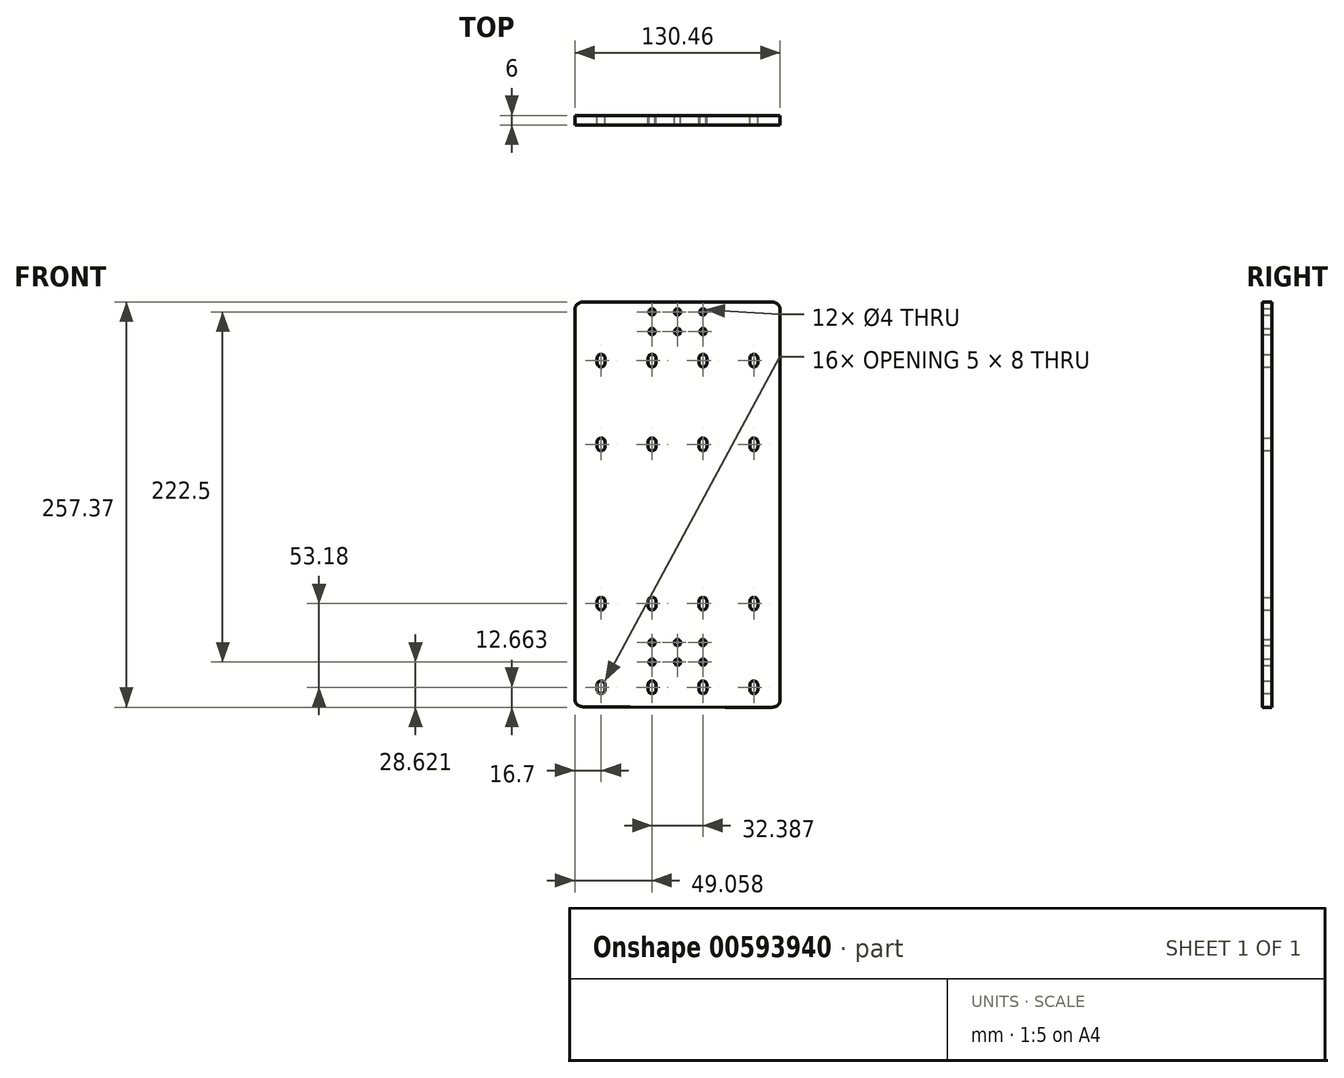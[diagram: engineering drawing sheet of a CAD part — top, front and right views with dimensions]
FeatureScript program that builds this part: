
annotation { "Feature Type Name" : "Feature", "Feature Type Description" : "" }
export const myFeature = defineFeature(function(context is Context, id is Id, definition is map)
    precondition{}
    {
        {
            var Q0;
            Q0=qCreatedBy(makeId("Front.planeOp"),FACE);
            var sketch = newSketch(context, id + "F0", { "sketchPlane" : qUnion([Q0])});
            skLineSegment(sketch, "E0.bottom", {"start": v(-82.55, 112.46) * mm, "end": v(-203.01, 112.46) * mm});
            skCircle(sketch, "E1", {"center": v(-142.78, 106.21) * mm, "radius": 2 * mm});
            skPoint(sketch, "E1.centerSnap0", {"position": v(-142.78, 112.46) * mm});
            skPoint(sketch, "E1.centerSnap1", {"position": v(-97.78, 99.96) * mm});
            skCircle(sketch, "E2.1.0.0", {"center": v(-126.61, 106.21) * mm, "radius": 2 * mm});
            skLineSegment(sketch, "E2.direction1", {"start": v(-142.78, 106.21) * mm, "end": v(-126.61, 106.21) * mm, "construction": true});
            skCircle(sketch, "E3.1.0.0", {"center": v(-158.95, 106.21) * mm, "radius": 2 * mm});
            skLineSegment(sketch, "E3.direction1", {"start": v(-142.78, 106.21) * mm, "end": v(-158.95, 106.21) * mm, "construction": true});
            skPoint(sketch, "E4", {"position": v(-97.78, 112.46) * mm});
            skCircle(sketch, "E5.2.1.0", {"center": v(-126.56, 93.71) * mm, "radius": 2 * mm});
            skCircle(sketch, "E5.2.1.1", {"center": v(-142.73, 93.71) * mm, "radius": 2 * mm});
            skCircle(sketch, "E5.2.1.2", {"center": v(-158.95, 93.71) * mm, "radius": 2 * mm});
            skLineSegment(sketch, "E5.direction1", {"start": v(-149.11, 106.21) * mm, "end": v(-149.11, 106.21) * mm});
            skLineSegment(sketch, "E5.direction2", {"start": v(-126.61, 106.21) * mm, "end": v(-126.56, 93.71) * mm, "construction": true});
            skLineSegment(sketch, "E6.bottom", {"start": v(-94.18, 79.25) * mm, "end": v(-94.4, 79.25) * mm});
            skLineSegment(sketch, "E6.top", {"start": v(-94.18, 71.25) * mm, "end": v(-94.4, 71.25) * mm});
            skLineSegment(sketch, "E6.left", {"start": v(-91.8, 76.87) * mm, "end": v(-91.8, 73.64) * mm});
            skLineSegment(sketch, "E6.right", {"start": v(-96.8, 76.87) * mm, "end": v(-96.8, 73.64) * mm});
            skPoint(sketch, "E7.visualSharp", {"position": v(-91.8, 79.25) * mm});
            skArc(sketch, "E7.filletArc", {"start": v(-91.8, 76.87) * mm, "mid": v(-92.49, 78.55) * mm, "end": v(-94.18, 79.25) * mm});
            skPoint(sketch, "E8.visualSharp", {"position": v(-91.8, 71.25) * mm});
            skArc(sketch, "E8.filletArc", {"start": v(-94.18, 71.25) * mm, "mid": v(-92.49, 71.95) * mm, "end": v(-91.8, 73.64) * mm});
            skPoint(sketch, "E9.visualSharp", {"position": v(-96.8, 71.25) * mm});
            skArc(sketch, "E9.filletArc", {"start": v(-96.8, 73.64) * mm, "mid": v(-96.1, 71.95) * mm, "end": v(-94.4, 71.25) * mm});
            skPoint(sketch, "E10.visualSharp", {"position": v(-96.8, 79.25) * mm});
            skArc(sketch, "E10.filletArc", {"start": v(-94.4, 79.25) * mm, "mid": v(-96.1, 78.55) * mm, "end": v(-96.8, 76.87) * mm});
            skPoint(sketch, "E11.0.1.0", {"position": v(-91.8, 26.07) * mm});
            skArc(sketch, "E11.0.1.1", {"start": v(-96.8, 20.46) * mm, "mid": v(-96.1, 18.77) * mm, "end": v(-94.4, 18.07) * mm});
            skArc(sketch, "E11.0.1.2", {"start": v(-91.8, 23.69) * mm, "mid": v(-92.49, 25.37) * mm, "end": v(-94.18, 26.07) * mm});
            skArc(sketch, "E11.0.1.3", {"start": v(-94.4, 26.07) * mm, "mid": v(-96.1, 25.37) * mm, "end": v(-96.8, 23.69) * mm});
            skPoint(sketch, "E11.0.1.4", {"position": v(-91.8, 18.07) * mm});
            skPoint(sketch, "E11.0.1.5", {"position": v(-96.8, 18.07) * mm});
            skLineSegment(sketch, "E11.0.1.6", {"start": v(-96.8, 23.69) * mm, "end": v(-96.8, 20.46) * mm});
            skArc(sketch, "E11.0.1.7", {"start": v(-94.18, 18.07) * mm, "mid": v(-92.49, 18.77) * mm, "end": v(-91.8, 20.46) * mm});
            skPoint(sketch, "E11.0.1.8", {"position": v(-96.8, 26.07) * mm});
            skLineSegment(sketch, "E11.0.1.9", {"start": v(-91.8, 23.69) * mm, "end": v(-91.8, 20.46) * mm});
            skLineSegment(sketch, "E11.0.1.10", {"start": v(-94.18, 18.07) * mm, "end": v(-94.4, 18.07) * mm});
            skLineSegment(sketch, "E11.0.1.11", {"start": v(-94.18, 26.07) * mm, "end": v(-94.4, 26.07) * mm});
            skPoint(sketch, "E11.1.0.0", {"position": v(-124.13, 79.25) * mm});
            skArc(sketch, "E11.1.0.1", {"start": v(-129.13, 73.64) * mm, "mid": v(-128.43, 71.95) * mm, "end": v(-126.74, 71.25) * mm});
            skArc(sketch, "E11.1.0.2", {"start": v(-124.13, 76.87) * mm, "mid": v(-124.83, 78.55) * mm, "end": v(-126.52, 79.25) * mm});
            skArc(sketch, "E11.1.0.3", {"start": v(-126.74, 79.25) * mm, "mid": v(-128.43, 78.55) * mm, "end": v(-129.13, 76.87) * mm});
            skPoint(sketch, "E11.1.0.4", {"position": v(-124.13, 71.25) * mm});
            skPoint(sketch, "E11.1.0.5", {"position": v(-129.13, 71.25) * mm});
            skLineSegment(sketch, "E11.1.0.6", {"start": v(-129.13, 76.87) * mm, "end": v(-129.13, 73.64) * mm});
            skArc(sketch, "E11.1.0.7", {"start": v(-126.52, 71.25) * mm, "mid": v(-124.83, 71.95) * mm, "end": v(-124.13, 73.64) * mm});
            skPoint(sketch, "E11.1.0.8", {"position": v(-129.13, 79.25) * mm});
            skLineSegment(sketch, "E11.1.0.9", {"start": v(-124.13, 76.87) * mm, "end": v(-124.13, 73.64) * mm});
            skLineSegment(sketch, "E11.1.0.10", {"start": v(-126.52, 71.25) * mm, "end": v(-126.74, 71.25) * mm});
            skLineSegment(sketch, "E11.1.0.11", {"start": v(-126.52, 79.25) * mm, "end": v(-126.74, 79.25) * mm});
            skPoint(sketch, "E11.1.1.0", {"position": v(-124.13, 26.07) * mm});
            skArc(sketch, "E11.1.1.1", {"start": v(-129.13, 20.46) * mm, "mid": v(-128.43, 18.77) * mm, "end": v(-126.74, 18.07) * mm});
            skArc(sketch, "E11.1.1.2", {"start": v(-124.13, 23.69) * mm, "mid": v(-124.83, 25.37) * mm, "end": v(-126.52, 26.07) * mm});
            skArc(sketch, "E11.1.1.3", {"start": v(-126.74, 26.07) * mm, "mid": v(-128.43, 25.37) * mm, "end": v(-129.13, 23.69) * mm});
            skPoint(sketch, "E11.1.1.4", {"position": v(-124.13, 18.07) * mm});
            skPoint(sketch, "E11.1.1.5", {"position": v(-129.13, 18.07) * mm});
            skLineSegment(sketch, "E11.1.1.6", {"start": v(-129.13, 23.69) * mm, "end": v(-129.13, 20.46) * mm});
            skArc(sketch, "E11.1.1.7", {"start": v(-126.52, 18.07) * mm, "mid": v(-124.83, 18.77) * mm, "end": v(-124.13, 20.46) * mm});
            skPoint(sketch, "E11.1.1.8", {"position": v(-129.13, 26.07) * mm});
            skLineSegment(sketch, "E11.1.1.9", {"start": v(-124.13, 23.69) * mm, "end": v(-124.13, 20.46) * mm});
            skLineSegment(sketch, "E11.1.1.10", {"start": v(-126.52, 18.07) * mm, "end": v(-126.74, 18.07) * mm});
            skLineSegment(sketch, "E11.1.1.11", {"start": v(-126.52, 26.07) * mm, "end": v(-126.74, 26.07) * mm});
            skPoint(sketch, "E11.2.0.0", {"position": v(-156.47, 79.25) * mm});
            skArc(sketch, "E11.2.0.1", {"start": v(-161.47, 73.64) * mm, "mid": v(-160.77, 71.95) * mm, "end": v(-159.08, 71.25) * mm});
            skArc(sketch, "E11.2.0.2", {"start": v(-156.47, 76.87) * mm, "mid": v(-157.17, 78.55) * mm, "end": v(-158.86, 79.25) * mm});
            skArc(sketch, "E11.2.0.3", {"start": v(-159.08, 79.25) * mm, "mid": v(-160.77, 78.55) * mm, "end": v(-161.47, 76.87) * mm});
            skPoint(sketch, "E11.2.0.4", {"position": v(-156.47, 71.25) * mm});
            skPoint(sketch, "E11.2.0.5", {"position": v(-161.47, 71.25) * mm});
            skLineSegment(sketch, "E11.2.0.6", {"start": v(-161.47, 76.87) * mm, "end": v(-161.47, 73.64) * mm});
            skArc(sketch, "E11.2.0.7", {"start": v(-158.86, 71.25) * mm, "mid": v(-157.17, 71.95) * mm, "end": v(-156.47, 73.64) * mm});
            skPoint(sketch, "E11.2.0.8", {"position": v(-161.47, 79.25) * mm});
            skLineSegment(sketch, "E11.2.0.9", {"start": v(-156.47, 76.87) * mm, "end": v(-156.47, 73.64) * mm});
            skLineSegment(sketch, "E11.2.0.10", {"start": v(-158.86, 71.25) * mm, "end": v(-159.08, 71.25) * mm});
            skLineSegment(sketch, "E11.2.0.11", {"start": v(-158.86, 79.25) * mm, "end": v(-159.08, 79.25) * mm});
            skPoint(sketch, "E11.2.1.0", {"position": v(-156.47, 26.07) * mm});
            skArc(sketch, "E11.2.1.1", {"start": v(-161.47, 20.46) * mm, "mid": v(-160.77, 18.77) * mm, "end": v(-159.08, 18.07) * mm});
            skArc(sketch, "E11.2.1.2", {"start": v(-156.47, 23.69) * mm, "mid": v(-157.17, 25.37) * mm, "end": v(-158.86, 26.07) * mm});
            skArc(sketch, "E11.2.1.3", {"start": v(-159.08, 26.07) * mm, "mid": v(-160.77, 25.37) * mm, "end": v(-161.47, 23.69) * mm});
            skPoint(sketch, "E11.2.1.4", {"position": v(-156.47, 18.07) * mm});
            skPoint(sketch, "E11.2.1.5", {"position": v(-161.47, 18.07) * mm});
            skLineSegment(sketch, "E11.2.1.6", {"start": v(-161.47, 23.69) * mm, "end": v(-161.47, 20.46) * mm});
            skArc(sketch, "E11.2.1.7", {"start": v(-158.86, 18.07) * mm, "mid": v(-157.17, 18.77) * mm, "end": v(-156.47, 20.46) * mm});
            skPoint(sketch, "E11.2.1.8", {"position": v(-161.47, 26.07) * mm});
            skLineSegment(sketch, "E11.2.1.9", {"start": v(-156.47, 23.69) * mm, "end": v(-156.47, 20.46) * mm});
            skLineSegment(sketch, "E11.2.1.10", {"start": v(-158.86, 18.07) * mm, "end": v(-159.08, 18.07) * mm});
            skLineSegment(sketch, "E11.2.1.11", {"start": v(-158.86, 26.07) * mm, "end": v(-159.08, 26.07) * mm});
            skPoint(sketch, "E11.3.0.0", {"position": v(-188.81, 79.25) * mm});
            skArc(sketch, "E11.3.0.1", {"start": v(-193.81, 73.64) * mm, "mid": v(-193.11, 71.95) * mm, "end": v(-191.42, 71.25) * mm});
            skArc(sketch, "E11.3.0.2", {"start": v(-188.81, 76.87) * mm, "mid": v(-189.5, 78.55) * mm, "end": v(-191.2, 79.25) * mm});
            skArc(sketch, "E11.3.0.3", {"start": v(-191.42, 79.25) * mm, "mid": v(-193.11, 78.55) * mm, "end": v(-193.81, 76.87) * mm});
            skPoint(sketch, "E11.3.0.4", {"position": v(-188.81, 71.25) * mm});
            skPoint(sketch, "E11.3.0.5", {"position": v(-193.81, 71.25) * mm});
            skLineSegment(sketch, "E11.3.0.6", {"start": v(-193.81, 76.87) * mm, "end": v(-193.81, 73.64) * mm});
            skArc(sketch, "E11.3.0.7", {"start": v(-191.2, 71.25) * mm, "mid": v(-189.5, 71.95) * mm, "end": v(-188.81, 73.64) * mm});
            skPoint(sketch, "E11.3.0.8", {"position": v(-193.81, 79.25) * mm});
            skLineSegment(sketch, "E11.3.0.9", {"start": v(-188.81, 76.87) * mm, "end": v(-188.81, 73.64) * mm});
            skLineSegment(sketch, "E11.3.0.10", {"start": v(-191.2, 71.25) * mm, "end": v(-191.42, 71.25) * mm});
            skLineSegment(sketch, "E11.3.0.11", {"start": v(-191.2, 79.25) * mm, "end": v(-191.42, 79.25) * mm});
            skPoint(sketch, "E11.3.1.0", {"position": v(-188.81, 26.07) * mm});
            skArc(sketch, "E11.3.1.1", {"start": v(-193.81, 20.46) * mm, "mid": v(-193.11, 18.77) * mm, "end": v(-191.42, 18.07) * mm});
            skArc(sketch, "E11.3.1.2", {"start": v(-188.81, 23.69) * mm, "mid": v(-189.5, 25.37) * mm, "end": v(-191.2, 26.07) * mm});
            skArc(sketch, "E11.3.1.3", {"start": v(-191.42, 26.07) * mm, "mid": v(-193.11, 25.37) * mm, "end": v(-193.81, 23.69) * mm});
            skPoint(sketch, "E11.3.1.4", {"position": v(-188.81, 18.07) * mm});
            skPoint(sketch, "E11.3.1.5", {"position": v(-193.81, 18.07) * mm});
            skLineSegment(sketch, "E11.3.1.6", {"start": v(-193.81, 23.69) * mm, "end": v(-193.81, 20.46) * mm});
            skArc(sketch, "E11.3.1.7", {"start": v(-191.2, 18.07) * mm, "mid": v(-189.5, 18.77) * mm, "end": v(-188.81, 20.46) * mm});
            skPoint(sketch, "E11.3.1.8", {"position": v(-193.81, 26.07) * mm});
            skLineSegment(sketch, "E11.3.1.9", {"start": v(-188.81, 23.69) * mm, "end": v(-188.81, 20.46) * mm});
            skLineSegment(sketch, "E11.3.1.10", {"start": v(-191.2, 18.07) * mm, "end": v(-191.42, 18.07) * mm});
            skLineSegment(sketch, "E11.3.1.11", {"start": v(-191.2, 26.07) * mm, "end": v(-191.42, 26.07) * mm});
            skLineSegment(sketch, "E11.direction1", {"start": v(-96.8, 71.25) * mm, "end": v(-129.13, 71.25) * mm, "construction": true});
            skLineSegment(sketch, "E11.direction2", {"start": v(-96.8, 71.25) * mm, "end": v(-96.8, 18.07) * mm, "construction": true});
            skPoint(sketch, "E12.0.1.0", {"position": v(-91.8, -128.25) * mm});
            skPoint(sketch, "E12.0.1.1", {"position": v(-91.8, -136.25) * mm});
            skPoint(sketch, "E12.0.1.2", {"position": v(-161.47, -75.07) * mm});
            skLineSegment(sketch, "E12.0.1.3", {"start": v(-96.8, -83.07) * mm, "end": v(-129.13, -83.07) * mm, "construction": true});
            skPoint(sketch, "E12.0.1.4", {"position": v(-161.47, -83.07) * mm});
            skPoint(sketch, "E12.0.1.5", {"position": v(-161.47, -128.25) * mm});
            skPoint(sketch, "E12.0.1.6", {"position": v(-193.81, -83.07) * mm});
            skPoint(sketch, "E12.0.1.7", {"position": v(-188.81, -136.25) * mm});
            skPoint(sketch, "E12.0.1.8", {"position": v(-193.81, -136.25) * mm});
            skPoint(sketch, "E12.0.1.9", {"position": v(-129.13, -75.07) * mm});
            skLineSegment(sketch, "E12.0.1.10", {"start": v(-96.8, -83.07) * mm, "end": v(-96.8, -136.25) * mm, "construction": true});
            skPoint(sketch, "E12.0.1.11", {"position": v(-91.8, -75.07) * mm});
            skPoint(sketch, "E12.0.1.12", {"position": v(-124.13, -75.07) * mm});
            skPoint(sketch, "E12.0.1.13", {"position": v(-96.8, -128.25) * mm});
            skPoint(sketch, "E12.0.1.14", {"position": v(-96.8, -75.07) * mm});
            skPoint(sketch, "E12.0.1.15", {"position": v(-188.81, -128.25) * mm});
            skPoint(sketch, "E12.0.1.16", {"position": v(-129.13, -128.25) * mm});
            skPoint(sketch, "E12.0.1.17", {"position": v(-193.81, -128.25) * mm});
            skPoint(sketch, "E12.0.1.18", {"position": v(-129.13, -83.07) * mm});
            skPoint(sketch, "E12.0.1.19", {"position": v(-91.8, -83.07) * mm});
            skPoint(sketch, "E12.0.1.20", {"position": v(-161.47, -136.25) * mm});
            skPoint(sketch, "E12.0.1.21", {"position": v(-96.8, -136.25) * mm});
            skPoint(sketch, "E12.0.1.22", {"position": v(-156.47, -75.07) * mm});
            skPoint(sketch, "E12.0.1.23", {"position": v(-129.13, -136.25) * mm});
            skPoint(sketch, "E12.0.1.24", {"position": v(-156.47, -136.25) * mm});
            skPoint(sketch, "E12.0.1.25", {"position": v(-124.13, -136.25) * mm});
            skPoint(sketch, "E12.0.1.26", {"position": v(-156.47, -128.25) * mm});
            skPoint(sketch, "E12.0.1.27", {"position": v(-124.13, -83.07) * mm});
            skPoint(sketch, "E12.0.1.28", {"position": v(-124.13, -128.25) * mm});
            skPoint(sketch, "E12.0.1.29", {"position": v(-193.81, -75.07) * mm});
            skPoint(sketch, "E12.0.1.30", {"position": v(-188.81, -75.07) * mm});
            skPoint(sketch, "E12.0.1.31", {"position": v(-156.47, -83.07) * mm});
            skPoint(sketch, "E12.0.1.32", {"position": v(-188.81, -83.07) * mm});
            skPoint(sketch, "E12.0.1.33", {"position": v(-96.8, -83.07) * mm});
            skLineSegment(sketch, "E12.0.1.34", {"start": v(-158.86, -128.25) * mm, "end": v(-159.08, -128.25) * mm});
            skArc(sketch, "E12.0.1.35", {"start": v(-96.8, -133.86) * mm, "mid": v(-96.1, -135.55) * mm, "end": v(-94.4, -136.25) * mm});
            skLineSegment(sketch, "E12.0.1.36", {"start": v(-193.81, -130.63) * mm, "end": v(-193.81, -133.86) * mm});
            skArc(sketch, "E12.0.1.37", {"start": v(-193.81, -133.86) * mm, "mid": v(-193.11, -135.55) * mm, "end": v(-191.42, -136.25) * mm});
            skArc(sketch, "E12.0.1.38", {"start": v(-191.2, -136.25) * mm, "mid": v(-189.5, -135.55) * mm, "end": v(-188.81, -133.86) * mm});
            skArc(sketch, "E12.0.1.39", {"start": v(-126.74, -128.25) * mm, "mid": v(-128.43, -128.95) * mm, "end": v(-129.13, -130.63) * mm});
            skArc(sketch, "E12.0.1.40", {"start": v(-158.86, -136.25) * mm, "mid": v(-157.17, -135.55) * mm, "end": v(-156.47, -133.86) * mm});
            skArc(sketch, "E12.0.1.41", {"start": v(-91.8, -130.63) * mm, "mid": v(-92.49, -128.95) * mm, "end": v(-94.18, -128.25) * mm});
            skLineSegment(sketch, "E12.0.1.42", {"start": v(-91.8, -77.45) * mm, "end": v(-91.8, -80.68) * mm});
            skArc(sketch, "E12.0.1.43", {"start": v(-126.52, -136.25) * mm, "mid": v(-124.83, -135.55) * mm, "end": v(-124.13, -133.86) * mm});
            skArc(sketch, "E12.0.1.44", {"start": v(-159.08, -128.25) * mm, "mid": v(-160.77, -128.95) * mm, "end": v(-161.47, -130.63) * mm});
            skArc(sketch, "E12.0.1.45", {"start": v(-94.18, -136.25) * mm, "mid": v(-92.49, -135.55) * mm, "end": v(-91.8, -133.86) * mm});
            skLineSegment(sketch, "E12.0.1.46", {"start": v(-94.18, -128.25) * mm, "end": v(-94.4, -128.25) * mm});
            skLineSegment(sketch, "E12.0.1.47", {"start": v(-191.2, -128.25) * mm, "end": v(-191.42, -128.25) * mm});
            skLineSegment(sketch, "E12.0.1.48", {"start": v(-126.52, -128.25) * mm, "end": v(-126.74, -128.25) * mm});
            skArc(sketch, "E12.0.1.49", {"start": v(-129.13, -133.86) * mm, "mid": v(-128.43, -135.55) * mm, "end": v(-126.74, -136.25) * mm});
            skArc(sketch, "E12.0.1.50", {"start": v(-161.47, -133.86) * mm, "mid": v(-160.77, -135.55) * mm, "end": v(-159.08, -136.25) * mm});
            skLineSegment(sketch, "E12.0.1.51", {"start": v(-188.81, -130.63) * mm, "end": v(-188.81, -133.86) * mm});
            skLineSegment(sketch, "E12.0.1.52", {"start": v(-91.8, -130.63) * mm, "end": v(-91.8, -133.86) * mm});
            skLineSegment(sketch, "E12.0.1.53", {"start": v(-124.13, -130.63) * mm, "end": v(-124.13, -133.86) * mm});
            skArc(sketch, "E12.0.1.54", {"start": v(-159.08, -75.07) * mm, "mid": v(-160.77, -75.77) * mm, "end": v(-161.47, -77.45) * mm});
            skLineSegment(sketch, "E12.0.1.55", {"start": v(-156.47, -130.63) * mm, "end": v(-156.47, -133.86) * mm});
            skArc(sketch, "E12.0.1.56", {"start": v(-124.13, -130.63) * mm, "mid": v(-124.83, -128.95) * mm, "end": v(-126.52, -128.25) * mm});
            skArc(sketch, "E12.0.1.57", {"start": v(-126.74, -75.07) * mm, "mid": v(-128.43, -75.77) * mm, "end": v(-129.13, -77.45) * mm});
            skLineSegment(sketch, "E12.0.1.58", {"start": v(-96.8, -77.45) * mm, "end": v(-96.8, -80.68) * mm});
            skArc(sketch, "E12.0.1.59", {"start": v(-94.18, -83.07) * mm, "mid": v(-92.49, -82.37) * mm, "end": v(-91.8, -80.68) * mm});
            skArc(sketch, "E12.0.1.60", {"start": v(-156.47, -77.45) * mm, "mid": v(-157.17, -75.77) * mm, "end": v(-158.86, -75.07) * mm});
            skArc(sketch, "E12.0.1.61", {"start": v(-191.42, -75.07) * mm, "mid": v(-193.11, -75.77) * mm, "end": v(-193.81, -77.45) * mm});
            skArc(sketch, "E12.0.1.62", {"start": v(-188.81, -130.63) * mm, "mid": v(-189.5, -128.95) * mm, "end": v(-191.2, -128.25) * mm});
            skArc(sketch, "E12.0.1.63", {"start": v(-191.42, -128.25) * mm, "mid": v(-193.11, -128.95) * mm, "end": v(-193.81, -130.63) * mm});
            skArc(sketch, "E12.0.1.64", {"start": v(-91.8, -77.45) * mm, "mid": v(-92.49, -75.77) * mm, "end": v(-94.18, -75.07) * mm});
            skLineSegment(sketch, "E12.0.1.65", {"start": v(-96.8, -130.63) * mm, "end": v(-96.8, -133.86) * mm});
            skArc(sketch, "E12.0.1.66", {"start": v(-96.8, -80.68) * mm, "mid": v(-96.1, -82.37) * mm, "end": v(-94.4, -83.07) * mm});
            skArc(sketch, "E12.0.1.67", {"start": v(-156.47, -130.63) * mm, "mid": v(-157.17, -128.95) * mm, "end": v(-158.86, -128.25) * mm});
            skLineSegment(sketch, "E12.0.1.68", {"start": v(-129.13, -130.63) * mm, "end": v(-129.13, -133.86) * mm});
            skLineSegment(sketch, "E12.0.1.69", {"start": v(-161.47, -130.63) * mm, "end": v(-161.47, -133.86) * mm});
            skArc(sketch, "E12.0.1.70", {"start": v(-94.4, -128.25) * mm, "mid": v(-96.1, -128.95) * mm, "end": v(-96.8, -130.63) * mm});
            skLineSegment(sketch, "E12.0.1.71", {"start": v(-191.2, -75.07) * mm, "end": v(-191.42, -75.07) * mm});
            skLineSegment(sketch, "E12.0.1.72", {"start": v(-158.86, -75.07) * mm, "end": v(-159.08, -75.07) * mm});
            skArc(sketch, "E12.0.1.73", {"start": v(-94.4, -75.07) * mm, "mid": v(-96.1, -75.77) * mm, "end": v(-96.8, -77.45) * mm});
            skArc(sketch, "E12.0.1.74", {"start": v(-124.13, -77.45) * mm, "mid": v(-124.83, -75.77) * mm, "end": v(-126.52, -75.07) * mm});
            skLineSegment(sketch, "E12.0.1.75", {"start": v(-126.52, -75.07) * mm, "end": v(-126.74, -75.07) * mm});
            skArc(sketch, "E12.0.1.76", {"start": v(-188.81, -77.45) * mm, "mid": v(-189.5, -75.77) * mm, "end": v(-191.2, -75.07) * mm});
            skLineSegment(sketch, "E12.0.1.77", {"start": v(-126.52, -83.07) * mm, "end": v(-126.74, -83.07) * mm});
            skArc(sketch, "E12.0.1.78", {"start": v(-126.52, -83.07) * mm, "mid": v(-124.83, -82.37) * mm, "end": v(-124.13, -80.68) * mm});
            skArc(sketch, "E12.0.1.79", {"start": v(-158.86, -83.07) * mm, "mid": v(-157.17, -82.37) * mm, "end": v(-156.47, -80.68) * mm});
            skLineSegment(sketch, "E12.0.1.80", {"start": v(-94.18, -75.07) * mm, "end": v(-94.4, -75.07) * mm});
            skArc(sketch, "E12.0.1.81", {"start": v(-161.47, -80.68) * mm, "mid": v(-160.77, -82.37) * mm, "end": v(-159.08, -83.07) * mm});
            skLineSegment(sketch, "E12.0.1.82", {"start": v(-161.47, -77.45) * mm, "end": v(-161.47, -80.68) * mm});
            skArc(sketch, "E12.0.1.83", {"start": v(-193.81, -80.68) * mm, "mid": v(-193.11, -82.37) * mm, "end": v(-191.42, -83.07) * mm});
            skArc(sketch, "E12.0.1.84", {"start": v(-129.13, -80.68) * mm, "mid": v(-128.43, -82.37) * mm, "end": v(-126.74, -83.07) * mm});
            skLineSegment(sketch, "E12.0.1.85", {"start": v(-94.18, -136.25) * mm, "end": v(-94.4, -136.25) * mm});
            skLineSegment(sketch, "E12.0.1.86", {"start": v(-129.13, -77.45) * mm, "end": v(-129.13, -80.68) * mm});
            skLineSegment(sketch, "E12.0.1.87", {"start": v(-193.81, -77.45) * mm, "end": v(-193.81, -80.68) * mm});
            skLineSegment(sketch, "E12.0.1.88", {"start": v(-188.81, -77.45) * mm, "end": v(-188.81, -80.68) * mm});
            skLineSegment(sketch, "E12.0.1.89", {"start": v(-156.47, -77.45) * mm, "end": v(-156.47, -80.68) * mm});
            skLineSegment(sketch, "E12.0.1.90", {"start": v(-158.86, -83.07) * mm, "end": v(-159.08, -83.07) * mm});
            skArc(sketch, "E12.0.1.91", {"start": v(-191.2, -83.07) * mm, "mid": v(-189.5, -82.37) * mm, "end": v(-188.81, -80.68) * mm});
            skLineSegment(sketch, "E12.0.1.92", {"start": v(-191.2, -83.07) * mm, "end": v(-191.42, -83.07) * mm});
            skLineSegment(sketch, "E12.0.1.93", {"start": v(-124.13, -77.45) * mm, "end": v(-124.13, -80.68) * mm});
            skLineSegment(sketch, "E12.0.1.94", {"start": v(-191.2, -136.25) * mm, "end": v(-191.42, -136.25) * mm});
            skLineSegment(sketch, "E12.0.1.95", {"start": v(-94.18, -83.07) * mm, "end": v(-94.4, -83.07) * mm});
            skLineSegment(sketch, "E12.0.1.96", {"start": v(-158.86, -136.25) * mm, "end": v(-159.08, -136.25) * mm});
            skLineSegment(sketch, "E12.0.1.97", {"start": v(-126.52, -136.25) * mm, "end": v(-126.74, -136.25) * mm});
            skLineSegment(sketch, "E12.direction1", {"start": v(-193.81, 18.07) * mm, "end": v(-168.81, 18.07) * mm, "construction": true});
            skLineSegment(sketch, "E12.direction2", {"start": v(-193.81, 18.07) * mm, "end": v(-193.81, -136.25) * mm, "construction": true});
            skLineSegment(sketch, "E13", {"start": v(-203.01, -144.57) * mm, "end": v(-173.01, -144.57) * mm});
            skLineSegment(sketch, "E14", {"start": v(-112.55, -144.9) * mm, "end": v(-82.55, -144.9) * mm});
            skLineSegment(sketch, "E15", {"start": v(-208.01, 107.46) * mm, "end": v(-208.01, -139.57) * mm});
            skLineSegment(sketch, "E16", {"start": v(-77.55, 107.46) * mm, "end": v(-77.55, -139.9) * mm});
            skPoint(sketch, "E17.visualSharp", {"position": v(-208.01, -144.57) * mm});
            skArc(sketch, "E17.filletArc", {"start": v(-208.01, -139.57) * mm, "mid": v(-206.55, -143.1) * mm, "end": v(-203.01, -144.57) * mm});
            skPoint(sketch, "E18.visualSharp", {"position": v(-77.55, -144.9) * mm});
            skArc(sketch, "E18.filletArc", {"start": v(-82.55, -144.9) * mm, "mid": v(-79.02, -143.44) * mm, "end": v(-77.55, -139.9) * mm});
            skPoint(sketch, "E19.visualSharp", {"position": v(-208.01, 112.46) * mm});
            skArc(sketch, "E19.filletArc", {"start": v(-203.01, 112.46) * mm, "mid": v(-206.55, 111) * mm, "end": v(-208.01, 107.46) * mm});
            skPoint(sketch, "E20.visualSharp", {"position": v(-77.55, 112.46) * mm});
            skArc(sketch, "E20.filletArc", {"start": v(-77.55, 107.46) * mm, "mid": v(-79.02, 111) * mm, "end": v(-82.55, 112.46) * mm});
            skLineSegment(sketch, "E21", {"start": v(-173.01, -144.57) * mm, "end": v(-112.55, -144.9) * mm});
            skPoint(sketch, "E22.0.1.0", {"position": v(-142.78, -97.54) * mm});
            skLineSegment(sketch, "E22.0.1.1", {"start": v(-126.61, -103.79) * mm, "end": v(-126.56, -116.29) * mm, "construction": true});
            skCircle(sketch, "E22.0.1.3", {"center": v(-158.95, -116.29) * mm, "radius": 2 * mm});
            skLineSegment(sketch, "E22.0.1.9", {"start": v(-142.78, -103.79) * mm, "end": v(-158.95, -103.79) * mm, "construction": true});
            skLineSegment(sketch, "E22.0.1.10", {"start": v(-142.78, -103.79) * mm, "end": v(-126.61, -103.79) * mm, "construction": true});
            skCircle(sketch, "E22.0.1.11", {"center": v(-142.78, -103.79) * mm, "radius": 2 * mm});
            skPoint(sketch, "E22.0.1.13", {"position": v(-142.78, -97.54) * mm});
            skCircle(sketch, "E22.0.1.15", {"center": v(-158.95, -103.79) * mm, "radius": 2 * mm});
            skCircle(sketch, "E22.0.1.16", {"center": v(-126.61, -103.79) * mm, "radius": 2 * mm});
            skCircle(sketch, "E22.0.1.18", {"center": v(-142.73, -116.29) * mm, "radius": 2 * mm});
            skCircle(sketch, "E22.0.1.19", {"center": v(-126.56, -116.29) * mm, "radius": 2 * mm});
            skLineSegment(sketch, "E22.direction1", {"start": v(-158.95, 93.71) * mm, "end": v(-133.95, 93.71) * mm, "construction": true});
            skLineSegment(sketch, "E22.direction2", {"start": v(-158.95, 93.71) * mm, "end": v(-158.95, -116.29) * mm, "construction": true});
            skSolve(sketch);
        }
        {
            var Q0;
            Q0=makeQuery(id+"F0.imprint","IMPRINT",FACE,{"disambiguationData":[TD([[makeQuery(id+"F0.imprint","IMPRINT",EDGE,{"derivedFrom":sQuery(id+"F0.wireOp",EDGE,"E0.bottom")}),1.0]])]});
            extrude(context, id + "F1", {"entities" : qUnion([Q0]), "depth" : 6 * mm, "offsetDistance" : 25 * mm});
        }
    });
